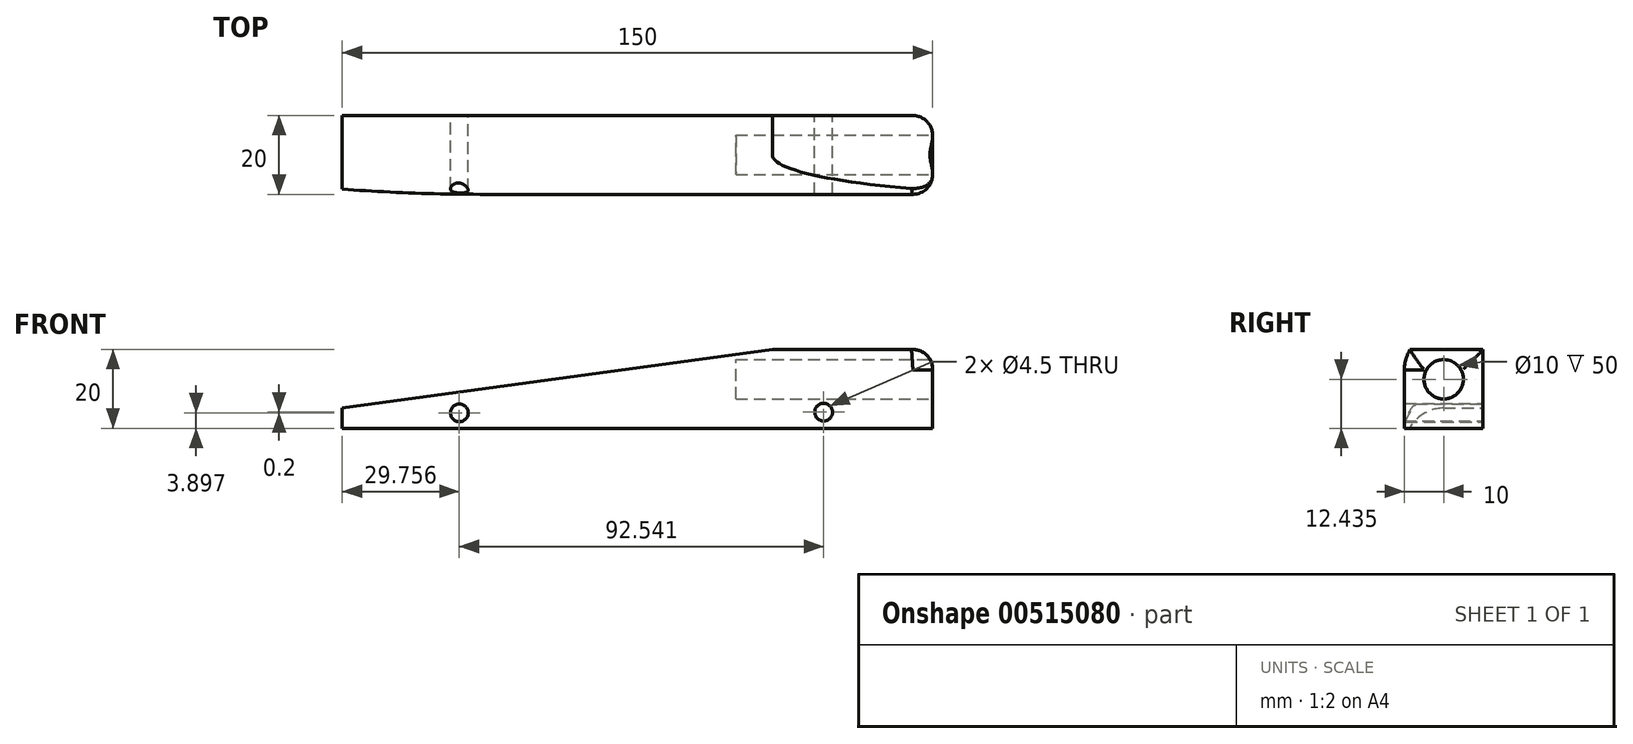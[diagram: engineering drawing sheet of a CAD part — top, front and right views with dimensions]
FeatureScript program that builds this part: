
annotation { "Feature Type Name" : "Feature", "Feature Type Description" : "" }
export const myFeature = defineFeature(function(context is Context, id is Id, definition is map)
    precondition{}
    {
        {
            var Q0;
            Q0=qCreatedBy(makeId("Top.planeOp"),FACE);
            var sketch = newSketch(context, id + "F0", { "sketchPlane" : qUnion([Q0])});
            skLineSegment(sketch, "E0.bottom", {"start": v(-21.9, 20) * mm, "end": v(128.1, 20) * mm});
            skLineSegment(sketch, "E0.top", {"start": v(-21.9, 0) * mm, "end": v(128.1, 0) * mm});
            skLineSegment(sketch, "E0.left", {"start": v(-21.9, 20) * mm, "end": v(-21.9, 0) * mm});
            skLineSegment(sketch, "E0.right", {"start": v(128.1, 20) * mm, "end": v(128.1, 0) * mm});
            skSolve(sketch);
        }
        {
            var Q0;
            Q0=makeQuery(id+"F0.imprint","IMPRINT",FACE,{"disambiguationData":[TD([[makeQuery(id+"F0.imprint","IMPRINT",EDGE,{"derivedFrom":sQuery(id+"F0.wireOp",EDGE,"E0.bottom")}),-1.0]])]});
            extrude(context, id + "F1", {"entities" : qUnion([Q0]), "depth" : 20 * mm, "offsetDistance" : 25 * mm});
        }
        {
            var Q0;
            Q0=makeQuery(id+"F1.opExtrude","SWEPT_FACE",FACE,{"disambiguationData":[OSD([sQuery(id+"F0.wireOp",EDGE,"E0.right")])]});
            var sketch = newSketch(context, id + "F2", { "sketchPlane" : qUnion([Q0])});
            skCircle(sketch, "E1", {"center": v(10, 12.43) * mm, "radius": 5 * mm});
            skPoint(sketch, "E1.centerSnap0", {"position": v(10, 0) * mm});
            skSolve(sketch);
        }
        {
            var Q0;
            Q0=makeQuery(id+"F2.imprint","IMPRINT",FACE,{"disambiguationData":[TD([[makeQuery(id+"F2.imprint","IMPRINT",EDGE,{"derivedFrom":sQuery(id+"F2.wireOp",EDGE,"E1")}),1.0]])]});
            extrude(context, id + "F3", {"entities" : qUnion([Q0]), "operationType" : NewBodyOperationType.REMOVE, "oppositeDirection" : true, "depth" : 50 * mm, "offsetDistance" : 25 * mm});
        }
        {
            var Q0;
            Q0=makeQuery(id+"F1.opExtrude","SWEPT_FACE",FACE,{"disambiguationData":[OSD([sQuery(id+"F0.wireOp",EDGE,"E0.bottom")])]});
            var sketch = newSketch(context, id + "F4", { "sketchPlane" : qUnion([Q0])});
            skCircle(sketch, "E2", {"center": v(-100.4, 4.1) * mm, "radius": 2.25 * mm});
            skCircle(sketch, "E3", {"center": v(-7.87, 3.9) * mm, "radius": 2.25 * mm});
            skSolve(sketch);
        }
        {
            var Q0;
            Q0=makeQuery(id+"F4.imprint","IMPRINT",FACE,{"disambiguationData":[TD([[makeQuery(id+"F4.imprint","IMPRINT",EDGE,{"derivedFrom":sQuery(id+"F4.wireOp",EDGE,"E2")}),1.0]])]});
            var Q1;
            Q1=makeQuery(id+"F4.imprint","IMPRINT",FACE,{"disambiguationData":[TD([[makeQuery(id+"F4.imprint","IMPRINT",EDGE,{"derivedFrom":sQuery(id+"F4.wireOp",EDGE,"E3")}),1.0]])]});
            extrude(context, id + "F5", {"entities" : qUnion([Q0, Q1]), "operationType" : NewBodyOperationType.REMOVE, "endBound" : BoundingType.THROUGH_ALL, "oppositeDirection" : true, "depth" : 25 * mm, "offsetDistance" : 25 * mm});
        }
        {
            var Q0;
            Q0=makeQuery(id+"F1.opExtrude","SWEPT_FACE",FACE,{"disambiguationData":[OSD([sQuery(id+"F0.wireOp",EDGE,"E0.bottom")])]});
            var sketch = newSketch(context, id + "F6", { "sketchPlane" : qUnion([Q0])});
            skLineSegment(sketch, "E4", {"start": v(21.9, 5.1) * mm, "end": v(-87.42, 20) * mm});
            skSolve(sketch);
        }
        {
            var Q0;
            {var subQ0=sQuery(id+"F6.wireOp",EDGE,"E4");Q0=makeQuery(id+"F6.imprint","IMPRINT",FACE,{"disambiguationData":[TD([[makeQuery(id+"F6.imprint","IMPRINT",EDGE,{"derivedFrom":subQ0}),-1.0]])]});}
            extrude(context, id + "F7", {"entities" : qUnion([Q0]), "operationType" : NewBodyOperationType.REMOVE, "endBound" : BoundingType.THROUGH_ALL, "oppositeDirection" : true, "depth" : 25 * mm, "offsetDistance" : 25 * mm});
        }
        {
            var Q0;
            Q0=makeQuery(id+"F7.boolean.opBoolean","INTERSECT",EDGE,{"derivedFrom":[makeQuery(id+"F1.opExtrude","SWEPT_FACE",FACE,{"disambiguationData":[OSD([sQuery(id+"F0.wireOp",EDGE,"E0.top")])]}),makeQuery(id+"F7.opExtrude","SWEPT_FACE",FACE,{"disambiguationData":[OSD([sQuery(id+"F6.wireOp",EDGE,"E4")])]})]});
            var Q1;
            Q1=makeQuery(id+"F7.boolean.opBoolean","COPY",EDGE,{"derivedFrom":makeQuery(id+"F7.opExtrude","CAP_EDGE",EDGE,{"disambiguationData":[OSD([sQuery(id+"F6.wireOp",EDGE,"E4")])],"isStart":true})});
            fillet(context, id + "F8", {"entities" : qUnion([Q0, Q1]), "radius" : 10 * mm, "tangentPropagation" : true, "allowEdgeOverflow" : false});
        }
        {
            var Q0;
            Q0=makeQuery(id+"F8.opFillet","BLEND_EDGE",EDGE,{"blendedFrom":[makeQuery(id+"F7.boolean.opBoolean","COPY",EDGE,{"derivedFrom":makeQuery(id+"F7.opExtrude","CAP_EDGE",EDGE,{"disambiguationData":[OSD([sQuery(id+"F6.wireOp",EDGE,"E4")])],"isStart":true})}),makeQuery(id+"F1.opExtrude","SWEPT_FACE",FACE,{"disambiguationData":[OSD([sQuery(id+"F0.wireOp",EDGE,"E0.left")])]})],"blendedInto":[makeQuery(id+"F1.opExtrude","SWEPT_FACE",FACE,{"disambiguationData":[OSD([sQuery(id+"F0.wireOp",EDGE,"E0.left")])]})]});
            var Q1;
            Q1=makeQuery(id+"F8.opFillet","BLEND_EDGE",EDGE,{"blendedFrom":[makeQuery(id+"F7.boolean.opBoolean","COPY",EDGE,{"derivedFrom":makeQuery(id+"F7.opExtrude","CAP_EDGE",EDGE,{"disambiguationData":[OSD([sQuery(id+"F6.wireOp",EDGE,"E4")])],"isStart":true})}),makeQuery(id+"F1.opExtrude","CAP_FACE",FACE,{"disambiguationData":[OSD([sQuery(id+"F0.wireOp",EDGE,"E0.bottom"),sQuery(id+"F0.wireOp",EDGE,"E0.top"),sQuery(id+"F0.wireOp",EDGE,"E0.left"),sQuery(id+"F0.wireOp",EDGE,"E0.right")])],"isStart":false})],"blendedInto":[makeQuery(id+"F1.opExtrude","CAP_FACE",FACE,{"disambiguationData":[OSD([sQuery(id+"F0.wireOp",EDGE,"E0.bottom"),sQuery(id+"F0.wireOp",EDGE,"E0.top"),sQuery(id+"F0.wireOp",EDGE,"E0.left"),sQuery(id+"F0.wireOp",EDGE,"E0.right")])],"isStart":false})]});
            var Q2;
            Q2=makeQuery(id+"F1.opExtrude","SWEPT_EDGE",EDGE,{"disambiguationData":[OSD([sQuery(id+"F0.wireOp",EDGE,"E0.bottom"),sQuery(id+"F0.wireOp",EDGE,"E0.right")])]});
            var Q3;
            Q3=makeQuery(id+"F1.opExtrude","SWEPT_EDGE",EDGE,{"disambiguationData":[OSD([sQuery(id+"F0.wireOp",EDGE,"E0.top"),sQuery(id+"F0.wireOp",EDGE,"E0.right")])]});
            var Q4;
            Q4=makeQuery(id+"F1.opExtrude","CAP_EDGE",EDGE,{"disambiguationData":[OSD([sQuery(id+"F0.wireOp",EDGE,"E0.right")])],"isStart":false});
            fillet(context, id + "F9", {"entities" : qUnion([Q0, Q1, Q2, Q3, Q4]), "radius" : 5 * mm, "tangentPropagation" : true, "allowEdgeOverflow" : false});
        }
    });
